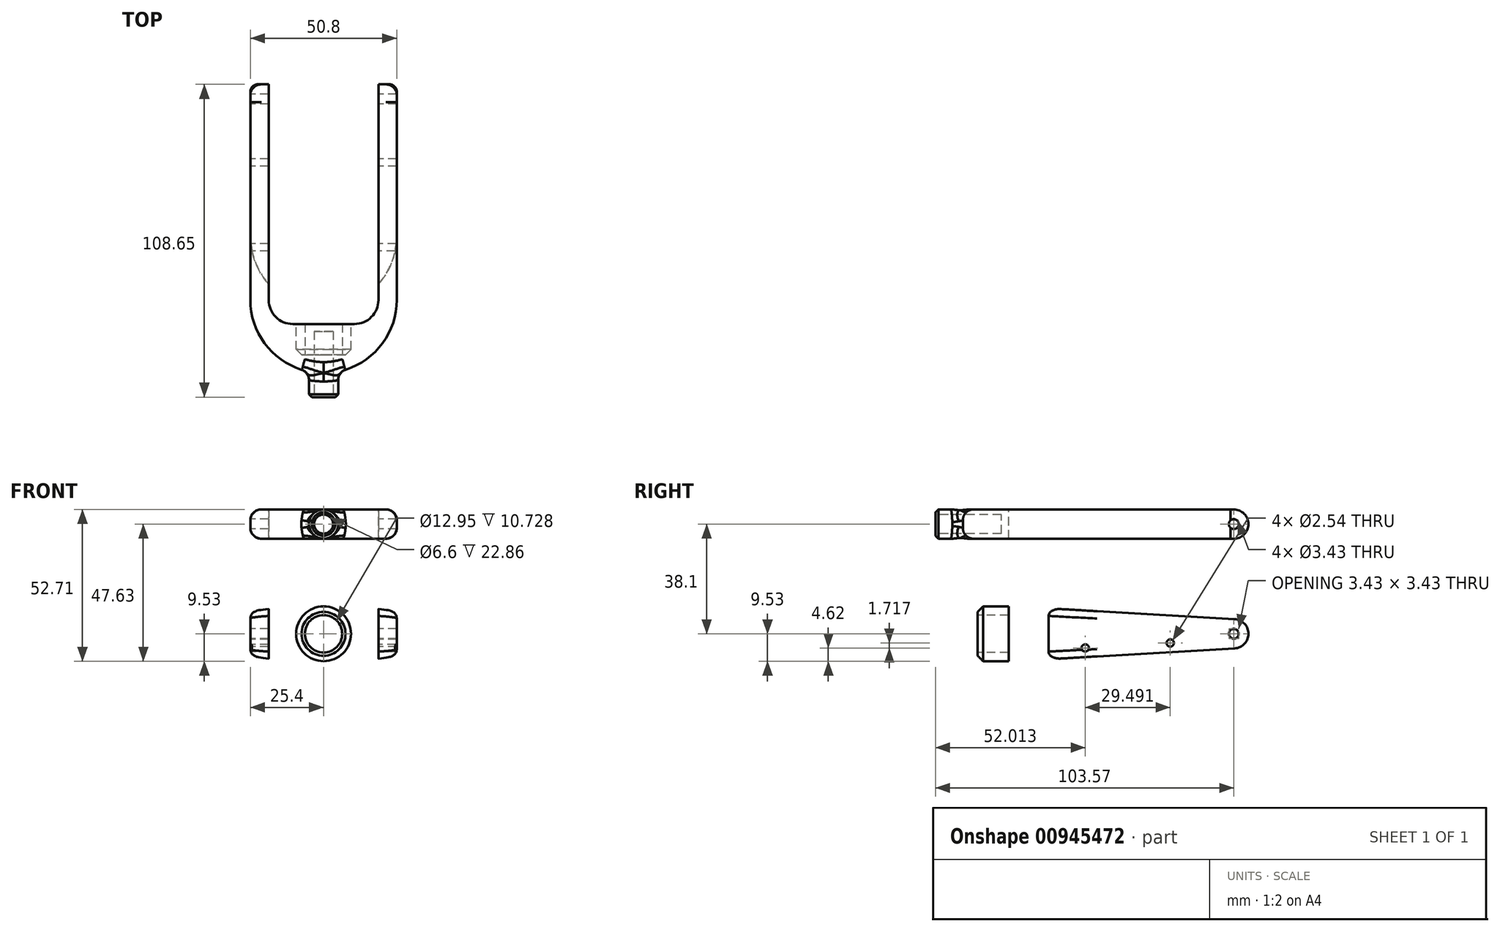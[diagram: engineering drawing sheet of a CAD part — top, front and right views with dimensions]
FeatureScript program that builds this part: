
annotation { "Feature Type Name" : "Feature", "Feature Type Description" : "" }
export const myFeature = defineFeature(function(context is Context, id is Id, definition is map)
    precondition{}
    {
        {
            var Q0;
            Q0=qCreatedBy(makeId("Right.planeOp"),FACE);
            var sketch = newSketch(context, id + "F0", { "sketchPlane" : qUnion([Q0])});
            skArc(sketch, "E0", {"start": v(0.3, -5.07) * mm, "mid": v(5.08, 0) * mm, "end": v(0.3, 5.07) * mm});
            skLineSegment(sketch, "E1", {"start": v(0.3, 5.07) * mm, "end": v(-76.2, 9.53) * mm});
            skLineSegment(sketch, "E2", {"start": v(-76.2, 9.53) * mm, "end": v(-76.2, -9.53) * mm});
            skLineSegment(sketch, "E3", {"start": v(-76.2, -9.53) * mm, "end": v(0.3, -5.07) * mm});
            skCircle(sketch, "E4", {"center": v(0, 0) * mm, "radius": 1.71 * mm});
            skCircle(sketch, "E5", {"center": v(-22.07, -3.2) * mm, "radius": 1.27 * mm});
            skCircle(sketch, "E6", {"center": v(-51.56, -4.9) * mm, "radius": 1.27 * mm});
            skSolve(sketch);
        }
        {
            var Q0;
            Q0=qSketchRegion(id+"F0",true);
            extrude(context, id + "F1", {"entities" : qUnion([Q0]), "depth" : 25.4 * mm, "hasSecondDirection" : true, "secondDirectionOppositeDirection" : true, "secondDirectionDepth" : 25.4 * mm});
        }
        {
            var Q0;
            Q0=qCreatedBy(makeId("Top.planeOp"),FACE);
            var sketch = newSketch(context, id + "F2", { "sketchPlane" : qUnion([Q0])});
            skLineSegment(sketch, "E7.bottom", {"start": v(-19.05, 5.65) * mm, "end": v(19.05, 5.65) * mm});
            skLineSegment(sketch, "E7.top", {"start": v(-10.67, -55.88) * mm, "end": v(10.67, -55.88) * mm});
            skLineSegment(sketch, "E7.left", {"start": v(-19.05, 5.65) * mm, "end": v(-19.05, -47.5) * mm});
            skLineSegment(sketch, "E7.right", {"start": v(19.05, 5.65) * mm, "end": v(19.05, -47.5) * mm});
            skPoint(sketch, "E8.visualSharp", {"position": v(-19.05, -55.88) * mm});
            skArc(sketch, "E8.filletArc", {"start": v(-19.05, -47.5) * mm, "mid": v(-16.6, -53.42) * mm, "end": v(-10.67, -55.88) * mm});
            skPoint(sketch, "E9.visualSharp", {"position": v(19.05, -55.88) * mm});
            skArc(sketch, "E9.filletArc", {"start": v(10.67, -55.88) * mm, "mid": v(16.6, -53.42) * mm, "end": v(19.05, -47.5) * mm});
            skArc(sketch, "E10", {"start": v(-25.4, -47.5) * mm, "mid": v(0, -72.9) * mm, "end": v(25.4, -47.5) * mm});
            skLineSegment(sketch, "E11", {"start": v(-25.4, -47.5) * mm, "end": v(-25.4, -76.2) * mm});
            skLineSegment(sketch, "E12", {"start": v(-25.4, -76.2) * mm, "end": v(25.4, -76.2) * mm});
            skLineSegment(sketch, "E13", {"start": v(25.4, -76.2) * mm, "end": v(25.4, -47.5) * mm});
            skSolve(sketch);
        }
        {
            var Q0;
            Q0=qSketchRegion(id+"F2",true);
            extrude(context, id + "F3", {"entities" : qUnion([Q0]), "operationType" : NewBodyOperationType.REMOVE, "endBound" : BoundingType.THROUGH_ALL, "oppositeDirection" : true, "depth" : 25.4 * mm, "hasSecondDirection" : true, "secondDirectionBound" : BoundingType.THROUGH_ALL, "secondDirectionOppositeDirection" : false, "secondDirectionDepth" : 25.4 * mm});
        }
        {
            var Q0;
            Q0=qCreatedBy(makeId("Right.planeOp"),FACE);
            var sketch = newSketch(context, id + "F4", { "sketchPlane" : qUnion([Q0])});
            skLineSegment(sketch, "E14", {"start": v(0, 0) * mm, "end": v(-108.54, 0) * mm, "construction": true});
            skSolve(sketch);
        }
        {
            var Q0;
            Q0=qCreatedBy(makeId("Right.planeOp"),FACE);
            var sketch = newSketch(context, id + "F5", { "sketchPlane" : qUnion([Q0])});
            skLineSegment(sketch, "E15", {"start": v(-55.88, 0) * mm, "end": v(-55.88, 8.9) * mm});
            skLineSegment(sketch, "E16", {"start": v(-88.9, 9.53) * mm, "end": v(-88.9, 0) * mm});
            skLineSegment(sketch, "E17", {"start": v(-88.9, 0) * mm, "end": v(-55.88, 0) * mm});
            skLineSegment(sketch, "E18", {"start": v(-55.88, 8.89) * mm, "end": v(-66.79, 9.53) * mm});
            skLineSegment(sketch, "E19", {"start": v(-66.79, 9.53) * mm, "end": v(-88.9, 9.53) * mm});
            skSolve(sketch);
        }
        {
            var Q0;
            Q0=qSketchRegion(id+"F5",true);
            var Q1;
            Q1=sQuery(id+"F4.wireOp",EDGE,"E14");
            revolve(context, id + "F6", {"operationType" : NewBodyOperationType.ADD, "entities" : qUnion([Q0]), "axis" : qUnion([Q1]), "revolveType" : RevolveType.FULL});
        }
        {
            var Q0;
            Q0=qCreatedBy(makeId("Right.planeOp"),FACE);
            var sketch = newSketch(context, id + "F7", { "sketchPlane" : qUnion([Q0])});
            skLineSegment(sketch, "E20", {"start": v(-88.9, 6.48) * mm, "end": v(-63.5, 6.48) * mm});
            skLineSegment(sketch, "E21", {"start": v(-63.5, 6.48) * mm, "end": v(-63.5, 5.59) * mm});
            skLineSegment(sketch, "E22", {"start": v(-63.5, 5.59) * mm, "end": v(-53.98, 5.59) * mm});
            skLineSegment(sketch, "E23", {"start": v(-53.98, 5.59) * mm, "end": v(-53.98, 0) * mm});
            skLineSegment(sketch, "E24", {"start": v(-88.9, 6.48) * mm, "end": v(-88.9, 0) * mm});
            skLineSegment(sketch, "E25", {"start": v(-88.9, 0) * mm, "end": v(-53.98, 0) * mm});
            skSolve(sketch);
        }
        {
            var Q0;
            Q0=qSketchRegion(id+"F7",true);
            var Q1;
            Q1=sQuery(id+"F4.wireOp",EDGE,"E14");
            revolve(context, id + "F8", {"operationType" : NewBodyOperationType.REMOVE, "entities" : qUnion([Q0]), "axis" : qUnion([Q1]), "revolveType" : RevolveType.FULL, "oppositeDirection" : true});
        }
        {
            var Q0;
            {var subQ0=sQuery(id+"F0.wireOp",EDGE,"E1");var subQ1=makeQuery(id+"F1.opExtrude","SWEPT_FACE",FACE,{"disambiguationData":[OSD([subQ0])]});var subQ2=makeQuery(id+"F3.opExtrude","SWEPT_FACE",FACE,{"disambiguationData":[OSD([sQuery(id+"F2.wireOp",EDGE,"E10")])]});Q0=makeQuery(id+"F6.boolean.opBoolean","SPLIT",EDGE,{"disambiguationData":[TD([makeQuery(id+"F1.opExtrude","CAP_FACE",FACE,{"disambiguationData":[OSD([sQuery(id+"F0.wireOp",EDGE,"E0"),subQ0,sQuery(id+"F0.wireOp",EDGE,"E2"),sQuery(id+"F0.wireOp",EDGE,"E3"),sQuery(id+"F0.wireOp",EDGE,"E4")])],"isStart":true})])],"derivedFrom":makeQuery(id+"F3.boolean.opBoolean","INTERSECT",EDGE,{"derivedFrom":[subQ1,subQ2]})});}
            var Q1;
            {var subQ0=sQuery(id+"F0.wireOp",EDGE,"E1");var subQ1=makeQuery(id+"F1.opExtrude","SWEPT_FACE",FACE,{"disambiguationData":[OSD([subQ0])]});var subQ2=makeQuery(id+"F3.opExtrude","SWEPT_FACE",FACE,{"disambiguationData":[OSD([sQuery(id+"F2.wireOp",EDGE,"E10")])]});Q1=makeQuery(id+"F6.boolean.opBoolean","SPLIT",EDGE,{"disambiguationData":[TD([makeQuery(id+"F1.opExtrude","CAP_FACE",FACE,{"disambiguationData":[OSD([sQuery(id+"F0.wireOp",EDGE,"E0"),subQ0,sQuery(id+"F0.wireOp",EDGE,"E2"),sQuery(id+"F0.wireOp",EDGE,"E3"),sQuery(id+"F0.wireOp",EDGE,"E4")])],"isStart":false})])],"derivedFrom":makeQuery(id+"F3.boolean.opBoolean","INTERSECT",EDGE,{"derivedFrom":[subQ1,subQ2]})});}
            var Q2;
            Q2=makeQuery(id+"F6.boolean.opBoolean","INTERSECT",EDGE,{"disambiguationData":[OD(0.0)],"derivedFrom":[makeQuery(id+"F3.boolean.opBoolean","COPY",FACE,{"derivedFrom":makeQuery(id+"F3.opExtrude","SWEPT_FACE",FACE,{"disambiguationData":[OSD([sQuery(id+"F2.wireOp",EDGE,"E10")])]})}),makeQuery(id+"F6.opRevolve","SWEPT_FACE",FACE,{"disambiguationData":[OSD([sQuery(id+"F5.wireOp",EDGE,"E19")])]})]});
            var Q3;
            Q3=makeQuery(id+"F6.boolean.opBoolean","INTERSECT",EDGE,{"disambiguationData":[OD(1.0)],"derivedFrom":[makeQuery(id+"F3.boolean.opBoolean","COPY",FACE,{"derivedFrom":makeQuery(id+"F3.opExtrude","SWEPT_FACE",FACE,{"disambiguationData":[OSD([sQuery(id+"F2.wireOp",EDGE,"E10")])]})}),makeQuery(id+"F6.opRevolve","SWEPT_FACE",FACE,{"disambiguationData":[OSD([sQuery(id+"F5.wireOp",EDGE,"E19")])]})]});
            fillet(context, id + "F9", {"entities" : qUnion([Q0, Q1, Q2, Q3]), "radius" : 2.54 * mm, "tangentPropagation" : true, "allowEdgeOverflow" : false});
        }
        {
            var Q0;
            Q0=makeQuery(id+"F6.opRevolve","SWEPT_EDGE",EDGE,{"disambiguationData":[OSD([sQuery(id+"F5.wireOp",EDGE,"E16"),sQuery(id+"F5.wireOp",EDGE,"E19")])]});
            chamfer(context, id + "F10", {"entities" : qUnion([Q0]), "width" : 1.9 * mm, "tangentPropagation" : true});
        }
        {
            var Q0;
            Q0=qCreatedBy(makeId("Right.planeOp"),FACE);
            var sketch = newSketch(context, id + "F11", { "sketchPlane" : qUnion([Q0])});
            skCircle(sketch, "E26", {"center": v(0, 38.1) * mm, "radius": 1.71 * mm});
            skArc(sketch, "E27", {"start": v(0, 33.02) * mm, "mid": v(5.08, 38.1) * mm, "end": v(0, 43.18) * mm});
            skLineSegment(sketch, "E28", {"start": v(0, 43.18) * mm, "end": v(-96.52, 43.18) * mm});
            skLineSegment(sketch, "E29", {"start": v(-96.52, 43.18) * mm, "end": v(-96.52, 33.02) * mm});
            skLineSegment(sketch, "E30", {"start": v(-96.52, 33.02) * mm, "end": v(0, 33.02) * mm});
            skSolve(sketch);
        }
        {
            var Q0;
            Q0=qSketchRegion(id+"F11",true);
            extrude(context, id + "F12", {"entities" : qUnion([Q0]), "depth" : 25.4 * mm, "hasSecondDirection" : true, "secondDirectionOppositeDirection" : true, "secondDirectionDepth" : 25.4 * mm});
        }
        {
            var Q0;
            Q0=makeQuery(id+"F12.opExtrude","SWEPT_FACE",FACE,{"disambiguationData":[OSD([sQuery(id+"F11.wireOp",EDGE,"E28")])]});
            var sketch = newSketch(context, id + "F13", { "sketchPlane" : qUnion([Q0])});
            skLineSegment(sketch, "E31.bottom", {"start": v(-19.05, 5.65) * mm, "end": v(19.05, 5.65) * mm});
            skLineSegment(sketch, "E31.top", {"start": v(-10.67, -78.17) * mm, "end": v(10.67, -78.17) * mm});
            skLineSegment(sketch, "E31.left", {"start": v(-19.05, 5.65) * mm, "end": v(-19.05, -69.79) * mm});
            skLineSegment(sketch, "E31.right", {"start": v(19.05, 5.65) * mm, "end": v(19.05, -69.79) * mm});
            skPoint(sketch, "E32.visualSharp", {"position": v(-19.05, -78.17) * mm});
            skArc(sketch, "E32.filletArc", {"start": v(-19.05, -69.79) * mm, "mid": v(-16.6, -75.72) * mm, "end": v(-10.67, -78.17) * mm});
            skPoint(sketch, "E33.visualSharp", {"position": v(19.05, -78.17) * mm});
            skArc(sketch, "E33.filletArc", {"start": v(10.67, -78.17) * mm, "mid": v(16.6, -75.72) * mm, "end": v(19.05, -69.79) * mm});
            skArc(sketch, "E34", {"start": v(-25.4, -69.79) * mm, "mid": v(0, -95.19) * mm, "end": v(25.4, -69.79) * mm});
            skLineSegment(sketch, "E35", {"start": v(-25.4, -69.79) * mm, "end": v(-25.4, -96.52) * mm});
            skLineSegment(sketch, "E36", {"start": v(-25.4, -96.52) * mm, "end": v(25.4, -96.52) * mm});
            skLineSegment(sketch, "E37", {"start": v(25.4, -96.52) * mm, "end": v(25.4, -69.79) * mm});
            skSolve(sketch);
        }
        {
            var Q0;
            Q0=qSketchRegion(id+"F13",true);
            extrude(context, id + "F14", {"entities" : qUnion([Q0]), "operationType" : NewBodyOperationType.REMOVE, "endBound" : BoundingType.THROUGH_ALL, "oppositeDirection" : true, "depth" : 25.4 * mm});
        }
        {
            var Q0;
            Q0=makeQuery(id+"F14.boolean.opBoolean","COPY",FACE,{"derivedFrom":makeQuery(id+"F14.opExtrude","SWEPT_FACE",FACE,{"disambiguationData":[OSD([sQuery(id+"F13.wireOp",EDGE,"E31.top")])]})});
            var sketch = newSketch(context, id + "F15", { "sketchPlane" : qUnion([Q0])});
            skCircle(sketch, "E38", {"center": v(0, 38.1) * mm, "radius": 5.08 * mm});
            skSolve(sketch);
        }
        {
            var Q0;
            Q0=qSketchRegion(id+"F15",true);
            extrude(context, id + "F16", {"entities" : qUnion([Q0]), "operationType" : NewBodyOperationType.ADD, "oppositeDirection" : true, "depth" : 25.4 * mm});
        }
        {
            var Q0;
            Q0=makeQuery(id+"F16.opExtrude","CAP_FACE",FACE,{"disambiguationData":[OSD([sQuery(id+"F15.wireOp",EDGE,"E38")])],"isStart":false});
            var sketch = newSketch(context, id + "F17", { "sketchPlane" : qUnion([Q0])});
            skCircle(sketch, "E39", {"center": v(0, 38.1) * mm, "radius": 3.3 * mm});
            skSolve(sketch);
        }
        {
            var Q0;
            Q0=qSketchRegion(id+"F17",true);
            extrude(context, id + "F18", {"entities" : qUnion([Q0]), "operationType" : NewBodyOperationType.REMOVE, "oppositeDirection" : true, "depth" : 22.86 * mm});
        }
        {
            var Q0;
            Q0=makeQuery(id+"F16.opExtrude","CAP_EDGE",EDGE,{"disambiguationData":[OSD([sQuery(id+"F15.wireOp",EDGE,"E38")])],"isStart":false});
            chamfer(context, id + "F19", {"entities" : qUnion([Q0]), "width" : 1.02 * mm, "tangentPropagation" : true});
        }
        {
            var Q0;
            Q0=makeQuery(id+"F12.opExtrude","CAP_EDGE",EDGE,{"disambiguationData":[OSD([sQuery(id+"F11.wireOp",EDGE,"E28")])],"isStart":true});
            var Q1;
            Q1=makeQuery(id+"F16.boolean.opBoolean","INTERSECT",EDGE,{"disambiguationData":[OD(0.0)],"derivedFrom":[makeQuery(id+"F14.boolean.opBoolean","COPY",FACE,{"derivedFrom":makeQuery(id+"F14.opExtrude","SWEPT_FACE",FACE,{"disambiguationData":[OSD([sQuery(id+"F13.wireOp",EDGE,"E34")])]})}),makeQuery(id+"F16.opExtrude","SWEPT_FACE",FACE,{"disambiguationData":[OSD([sQuery(id+"F15.wireOp",EDGE,"E38")])]})]});
            var Q2;
            Q2=makeQuery(id+"F16.boolean.opBoolean","INTERSECT",EDGE,{"disambiguationData":[OD(1.0)],"derivedFrom":[makeQuery(id+"F14.boolean.opBoolean","COPY",FACE,{"derivedFrom":makeQuery(id+"F14.opExtrude","SWEPT_FACE",FACE,{"disambiguationData":[OSD([sQuery(id+"F13.wireOp",EDGE,"E34")])]})}),makeQuery(id+"F16.opExtrude","SWEPT_FACE",FACE,{"disambiguationData":[OSD([sQuery(id+"F15.wireOp",EDGE,"E38")])]})]});
            var Q3;
            {var subQ0=sQuery(id+"F11.wireOp",EDGE,"E28");var subQ1=sQuery(id+"F13.wireOp",EDGE,"E34");Q3=makeQuery(id+"F16.boolean.opBoolean","SPLIT",EDGE,{"disambiguationData":[TD([makeQuery(id+"F12.opExtrude","CAP_FACE",FACE,{"disambiguationData":[OSD([sQuery(id+"F11.wireOp",EDGE,"E26"),sQuery(id+"F11.wireOp",EDGE,"E27"),subQ0,sQuery(id+"F11.wireOp",EDGE,"E29"),sQuery(id+"F11.wireOp",EDGE,"E30")])],"isStart":false})])],"derivedFrom":makeQuery(id+"F14.boolean.opBoolean","COPY",EDGE,{"derivedFrom":makeQuery(id+"F14.opExtrude","CAP_EDGE",EDGE,{"disambiguationData":[OSD([subQ1])],"isStart":true})})});}
            fillet(context, id + "F20", {"entities" : qUnion([Q0, Q1, Q2, Q3]), "radius" : 3.8 * mm, "tangentPropagation" : true, "allowEdgeOverflow" : false});
        }
        {
            var Q0;
            Q0=qCreatedBy(makeId("Top.planeOp"),FACE);
            var sketch = newSketch(context, id + "F21", { "sketchPlane" : qUnion([Q0])});
            skCircle(sketch, "E40", {"center": v(0, -58.17) * mm, "radius": 2.54 * mm});
            skSolve(sketch);
        }
        {
            var Q0;
            Q0=qSketchRegion(id+"F21",true);
            extrude(context, id + "F22", {"entities" : qUnion([Q0]), "operationType" : NewBodyOperationType.REMOVE, "endBound" : BoundingType.THROUGH_ALL, "oppositeDirection" : true, "depth" : 25.4 * mm});
        }
    });
